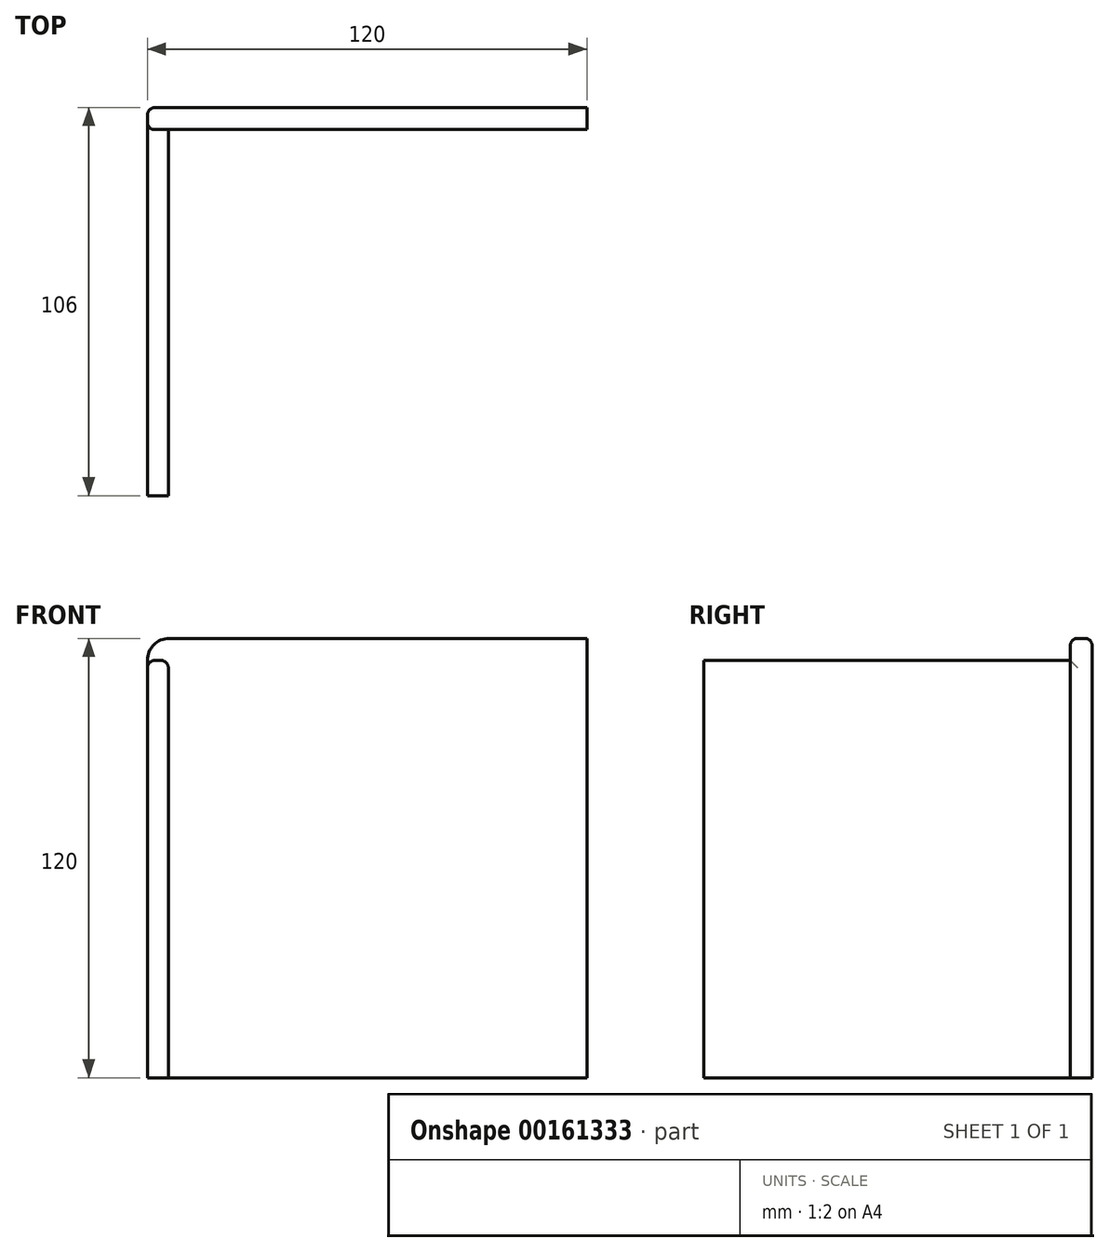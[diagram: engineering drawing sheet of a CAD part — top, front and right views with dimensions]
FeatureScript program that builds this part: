
annotation { "Feature Type Name" : "Feature", "Feature Type Description" : "" }
export const myFeature = defineFeature(function(context is Context, id is Id, definition is map)
    precondition{}
    {
        {
            var Q0;
            Q0=qCreatedBy(makeId("Front.planeOp"),FACE);
            var sketch = newSketch(context, id + "F0", { "sketchPlane" : qUnion([Q0])});
            skLineSegment(sketch, "E0.bottom", {"start": v(-56.32, 48.67) * mm, "end": v(63.68, 48.67) * mm});
            skLineSegment(sketch, "E0.top", {"start": v(-56.32, -71.33) * mm, "end": v(63.68, -71.33) * mm});
            skLineSegment(sketch, "E0.left", {"start": v(-56.32, 48.67) * mm, "end": v(-56.32, -71.33) * mm});
            skLineSegment(sketch, "E0.right", {"start": v(63.68, 48.67) * mm, "end": v(63.68, -71.33) * mm});
            skSolve(sketch);
        }
        {
            var Q0;
            Q0=makeQuery(id+"F0.imprint","IMPRINT",FACE,{"disambiguationData":[TD([[makeQuery(id+"F0.imprint","IMPRINT",EDGE,{"derivedFrom":sQuery(id+"F0.wireOp",EDGE,"E0.bottom")}),-1.0]])]});
            extrude(context, id + "F1", {"entities" : qUnion([Q0]), "depth" : 6 * mm});
        }
        {
            var Q0;
            Q0=makeQuery(id+"F1.opExtrude","SWEPT_EDGE",EDGE,{"disambiguationData":[OSD([sQuery(id+"F0.wireOp",EDGE,"E0.bottom"),sQuery(id+"F0.wireOp",EDGE,"E0.left")])]});
            fillet(context, id + "F2", {"entities" : qUnion([Q0]), "radius" : 6 * mm, "tangentPropagation" : true, "allowEdgeOverflow" : false});
        }
        {
            var Q0;
            Q0=makeQuery(id+"F1.opExtrude","CAP_FACE",FACE,{"disambiguationData":[OSD([sQuery(id+"F0.wireOp",EDGE,"E0.bottom"),sQuery(id+"F0.wireOp",EDGE,"E0.top"),sQuery(id+"F0.wireOp",EDGE,"E0.left"),sQuery(id+"F0.wireOp",EDGE,"E0.right")])],"isStart":false});
            var sketch = newSketch(context, id + "F3", { "sketchPlane" : qUnion([Q0])});
            skLineSegment(sketch, "E1", {"start": v(-50.6, -71.33) * mm, "end": v(-50.6, 42.67) * mm});
            skLineSegment(sketch, "E2", {"start": v(-50.6, 42.67) * mm, "end": v(-56.32, 42.67) * mm});
            skSolve(sketch);
        }
        {
            var Q0;
            {var subQ0=sQuery(id+"F3.wireOp",EDGE,"E1");Q0=makeQuery(id+"F3.imprint","IMPRINT",FACE,{"disambiguationData":[TD([[makeQuery(id+"F3.imprint","IMPRINT",EDGE,{"derivedFrom":subQ0}),1.0]])]});}
            extrude(context, id + "F4", {"entities" : qUnion([Q0]), "operationType" : NewBodyOperationType.ADD, "depth" : 100 * mm});
        }
        {
            var Q0;
            Q0=makeQuery(id+"F4.opExtrude","SWEPT_EDGE",EDGE,{"disambiguationData":[OSD([sQuery(id+"F0.wireOp",EDGE,"E0.left"),sQuery(id+"F3.wireOp",EDGE,"E2")])]});
            var Q1;
            Q1=makeQuery(id+"F4.opExtrude","SWEPT_EDGE",EDGE,{"disambiguationData":[OSD([sQuery(id+"F3.wireOp",EDGE,"E1"),sQuery(id+"F3.wireOp",EDGE,"E2")])]});
            fillet(context, id + "F5", {"entities" : qUnion([Q0, Q1]), "radius" : 2 * mm, "tangentPropagation" : true, "allowEdgeOverflow" : false});
        }
        {
            var Q0;
            Q0=makeQuery(id+"F1.opExtrude","CAP_EDGE",EDGE,{"disambiguationData":[OSD([sQuery(id+"F0.wireOp",EDGE,"E0.bottom")])],"isStart":false});
            var Q1;
            Q1=makeQuery(id+"F1.opExtrude","CAP_EDGE",EDGE,{"disambiguationData":[OSD([sQuery(id+"F0.wireOp",EDGE,"E0.bottom")])],"isStart":true});
            fillet(context, id + "F6", {"entities" : qUnion([Q0, Q1]), "radius" : 2 * mm, "tangentPropagation" : true, "allowEdgeOverflow" : false});
        }
    });
